# Revit family: Шаровой кран с удлиненным шпинделем и рычажной рукояткой 2190
name_source: partatom
category: Rohrzubehör
revit_build: Autodesk Revit 2018 (Build: 20190510_1515(x64)
units: mm (PartAtom-declared; Revit-internal decimal feet)

## family parameters
Arbeitsebenenbasiert = Nein
Beim Laden mit Abzugskörper schneiden = Nein
Bemaßung runder Anschluss = Durchmesser verwenden
Gemeinsam genutzt = Nein
Immer vertikal = Ja
OmniClass-Nummer = 23.65.55.14
OmniClass-Titel = Valves for Liquid Services
Teiletyp = Unterbricht

## types (1)
- Шаровой кран с удлиненным шпинделем и рычажной рукояткой 2190
    Hersteller = HERZ Armaturen Ges.m.b.H
    SCRNCODE = 05;10;02
    SCRNSEQ = ARM;ARM_TYP="ABVS";2
    URL = www.herz-armaturen.ru
    W01 = 135.00°
    Внутренняя резьба = в соответствии с ISO 228
    Корпус = штампованная латунь в соответствии с EN 12165, устойчивая к селективной цинковой коррозии, CW602N
    Макс. кратковременная температурная нагрузка = 150 °C
    Макс. рабочая температура = 130 °C
    Макс. рабочая температура (вода - не пар) = 110 °C
    Макс. рабочее давление = 2500000.0 Pa
    Мин. кратковременная температурная нагрузка = -50 °C
    Мин. рабочая температура = -10 °C
    Мин. рабочая температура (вода) = 1 °C
    Область применения = Шаровой кран  повышенной прочности с удлиненным шпинделем и рычажной рукояткой предназначен для систем отопления и охлаждения, которые должны выдерживать постоянное изменение рабочих параметров системы. Удлиненный шпиндель позволяет устанавливать более толстые слои изоляции. Корпус выполнен из латуни, устойчивой к селективной цинковой коррозии, CW602N. Шаровой кран является двунаправленным, поэтому движение среды возможно в обоих направлениях.
    Применение = Шаровые краны используются для перекрытия трубопроводов систем отопления и холодоснабжения. Шаровые краны не должны использоваться в качестве регулирующей арматуры, поэтому они должны быть полностью открыты или закрыты.
    Рукоятка = Рычажная рукоятка, цвет - красный, из оцинкованной стали
    Среда = Качество теплоносителя в соответствии с ÖNORM H5195 и/или предписаниями VDI 2035.
Разрешается использование смеси этилен или пропиленгликоля в соотношении 25-50% с водой.
    Уплотнение шара = PTFE
    Уплотнение шпинделя = EPDM
    Шар = штампованная латунь в соответствии с EN 12165, хромированный полнопроходной шар, CW617N
    Шпиндель = латунь в соответствии с 12164, CW614N
